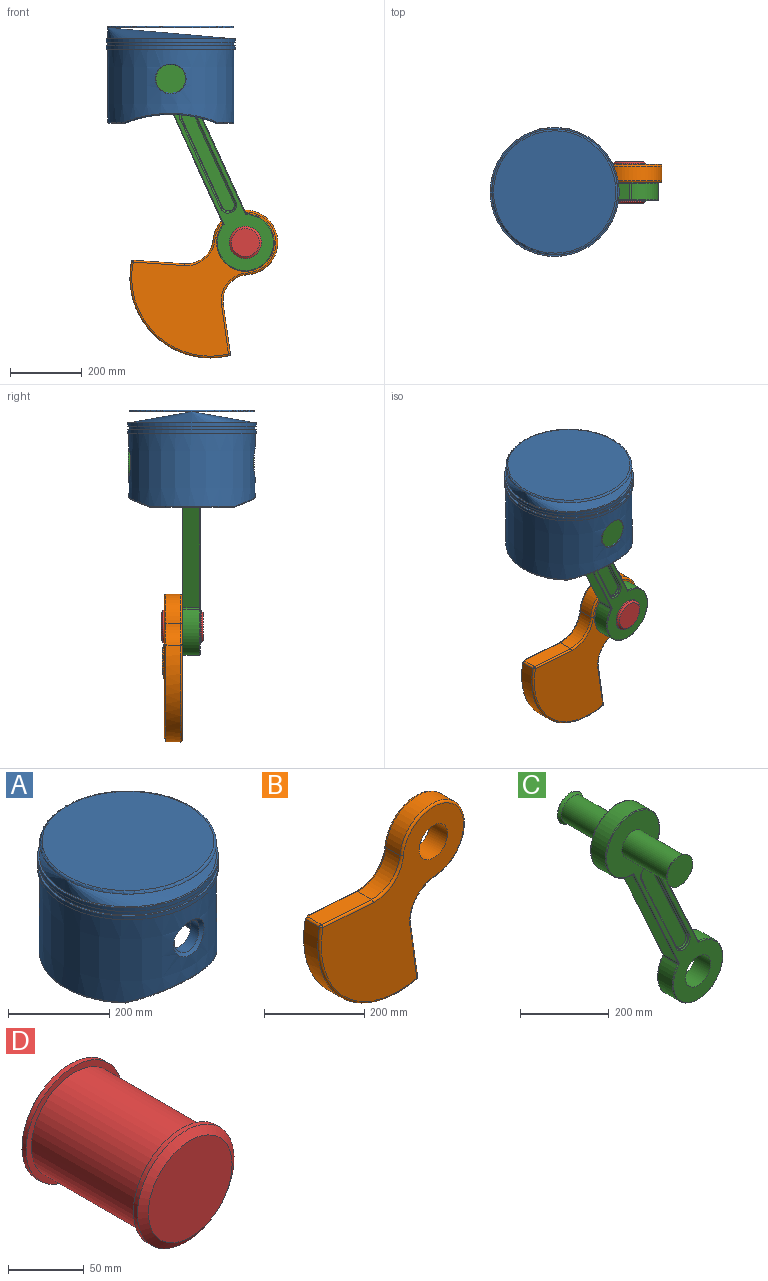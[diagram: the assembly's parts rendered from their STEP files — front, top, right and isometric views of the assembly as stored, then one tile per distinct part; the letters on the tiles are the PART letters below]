
ASSEMBLY  parts=4 mates=3
PART A: 29 faces, bbox 380.7x379x273.5 mm
  f0: cone r=175mm half-angle=0.2deg, axis (0,0,-1), area 12105mm2, adj f2,f7
  f1: plane 358.23x358.23mm, normal (0,0,1), area 4465.4mm2, adj f3,f5
  f2: plane 358.23x358.23mm, normal (0,0,-1), area 4437.3mm2, adj f0,f3
  f3: cylinder r=179.11mm len=358.23mm, axis (0,0,-1), area 10128.6mm2, adj f1,f2
  f4: plane 340.03x340.03mm, normal (0,0,1), area 90807.2mm2, adj f28
  f5: cone r=175mm half-angle=0.2deg, axis (0,0,-1), area 33563.3mm2, adj f1,f28
  f6: cylinder r=179.17mm len=358.34mm, axis (0,0,-1), area 10131.9mm2, adj f7,f8
  f7: plane 358.34x358.34mm, normal (0,0,1), area 4466.8mm2, adj f0,f6
  f8: plane 358.34x358.34mm, normal (0,0,-1), area 4438.7mm2, adj f6,f17
  f9: plane 291.53x291.53mm, normal (0,0,-1), area 66752.7mm2, adj f10
  f10: cylinder r=145.77mm len=291.53mm, axis (0,0,-1), area 181854.5mm2, adj f9,f15,f16,f24,f25,f26,f27
  f11: cylinder r=340mm len=251.53mm, axis (0,-1,0), area 7148.9mm2, adj f12,f14,f20,f25,f26,f27
  f12: plane 236.41x47.17mm, normal (0,0,-1), area 5172.1mm2, adj f11,f13,f20,f22,f23,f26
  f13: cylinder r=340mm len=251.53mm, axis (0,-1,0), area 7149.1mm2, adj f12,f14,f23,f24,f25,f26
  f14: plane 236.41x47.17mm, normal (0,0,-1), area 5172.1mm2, adj f11,f13,f20,f21,f23,f25
  f15: cylinder r=35mm len=70mm, axis (0,1,0), area 4846.2mm2, adj f10,f19
  f16: cylinder r=35mm len=70mm, axis (0,1,0), area 4846.2mm2, adj f10,f18
  f17: cone r=175mm half-angle=0.2deg, axis (0,0,-1), area 212035.7mm2, adj f8,f18,f19,f20,f21,f22,f23
  f18: bspline ~85.68x82.59mm, area 2302.6mm2, adj f16,f17
  f19: bspline ~85.68x82.59mm, area 2302.7mm2, adj f15,f17
  f20: bspline ~267.17x64.69mm, area 1460.4mm2, adj f11,f12,f14,f17,f21,f22
  f21: torus R=172.76mm, axis (0,0,1), area 1239.7mm2, adj f14,f17,f20,f23
  f22: torus R=172.76mm, axis (0,0,1), area 1239.7mm2, adj f12,f17,f20,f23
  f23: bspline ~267.17x64.69mm, area 1460.4mm2, adj f12,f13,f14,f17,f21,f22
  f24: bspline ~256.88x77.99mm, area 1310.8mm2, adj f10,f13,f25,f26
  f25: torus R=148.77mm, axis (0,0,1), area 772.3mm2, adj f10,f11,f13,f14,f24,f27
  f26: torus R=148.77mm, axis (0,0,1), area 772.3mm2, adj f10,f11,f12,f13,f24,f27
  f27: bspline ~256.88x77.99mm, area 1310.8mm2, adj f10,f11,f25,f26
  f28: torus R=170.01mm, axis (0,0,-1), area 8531.3mm2, adj f4,f5
PART B: 35 faces, bbox 450x60.6x491.2 mm
  f0: cylinder r=71.83mm len=81.86mm, axis (0,1,0), area 4750.8mm2, adj f1,f5,f21,f32
  f1: cylinder r=90mm len=179.84mm, axis (0,1,0), area 16411.5mm2, adj f0,f2,f19,f29
  f2: cylinder r=75mm len=79.87mm, axis (0,1,0), area 4637.4mm2, adj f1,f3,f18,f26
  f3: plane 142.02x40mm, normal (0.07,0,1), area 5677.6mm2, adj f2,f20,f22,f24,f25
  f4: cylinder r=223.85mm len=275.43mm, axis (0,1,0), area 17912.3mm2, adj f17,f22,f24,f27,f30,f31
  f5: plane 137.78x40mm, normal (0.99,0,0.14), area 5550.2mm2, adj f0,f23,f27,f30,f34
  f6: plane 401.08x401.08mm, normal (0,-1,0), area 75958.5mm2, adj f8,f25,f26,f29,f31,f32,f34
  f7: plane 392.34x392.34mm, normal (0,1,0), area 65113mm2, adj f8,f9,f17,f18,f19,f20,f21,f23
  f8: cylinder r=40mm len=80mm, axis (0,1,0), area 12566.4mm2, adj f6,f7
  f9: cylinder r=47.5mm len=95mm, axis (0,-1,0), area 895.4mm2, adj f7,f10
  f10: plane 95x95mm, normal (0,1,0), area 2670.4mm2, adj f9,f11
  f11: cylinder r=37.5mm len=75mm, axis (0,-1,0), area 706.9mm2, adj f10,f12
  f12: plane 75x75mm, normal (0,1,0), area 355.7mm2, adj f11,f14
  f13: plane 60x60mm, normal (0,1,0), area 2777.2mm2, adj f14,f16
  f14: cone r=30mm half-angle=50deg, axis (0,1,0), area 1611.9mm2, adj f12,f13
  f15: plane 2x2mm, normal (0,1,0), area 3.1mm2, adj f16
  f16: cone r=1mm half-angle=45deg, axis (0,1,0), area 66.6mm2, adj f13,f15
  f17: cone r=223.85mm half-angle=70deg, axis (0,-1,0), area 6357.7mm2, adj f4,f7,f20,f22,f23,f27
  f18: torus R=80mm, axis (0,-1,0), area 932.6mm2, adj f2,f7,f19,f20
  f19: torus R=85mm, axis (0,-1,0), area 3157.3mm2, adj f1,f7,f18,f21
  f20: cylinder r=5mm len=133.58mm, axis (-1,0,0.07), area 1046.3mm2, adj f3,f7,f17,f18,f22
  f21: torus R=76.83mm, axis (0,-1,0), area 956.4mm2, adj f0,f7,f19,f23
  f22: bspline ~80.83x33.21mm, area 98.9mm2, adj f3,f4,f17,f20,f24
  f23: cylinder r=5mm len=129.8mm, axis (-0.14,0,0.99), area 1021.6mm2, adj f5,f7,f17,f21,f27
  f24: cylinder r=5mm len=39.98mm, axis (0,1,0), area 278.7mm2, adj f3,f4,f22,f28
  f25: cylinder r=5mm len=142.37mm, axis (1,0,-0.07), area 1118.1mm2, adj f3,f6,f26,f28
  f26: torus R=80mm, axis (0,-1,0), area 932.6mm2, adj f2,f6,f25,f29
  f27: bspline ~123.64x49.12mm, area 100.3mm2, adj f4,f5,f17,f23,f30
  f28: sphere r=5mm, area 36.1mm2, adj f24,f25,f31
  f29: torus R=85mm, axis (0,-1,0), area 3157.3mm2, adj f1,f6,f26,f32
  f30: cylinder r=5mm len=39.99mm, axis (0,1,0), area 283.1mm2, adj f4,f5,f27,f33
  f31: torus R=218.85mm, axis (0,-1,0), area 3488.5mm2, adj f4,f6,f28,f33
  f32: torus R=76.83mm, axis (0,-1,0), area 956.4mm2, adj f0,f6,f29,f34
  f33: sphere r=5mm, area 38.3mm2, adj f30,f31,f34
  f34: cylinder r=5mm len=138.49mm, axis (0.14,0,-0.99), area 1093.1mm2, adj f5,f6,f32,f33
PART C: 61 faces, bbox 387.3x350x634.5 mm
  f0: plane 616.87x369.59mm, normal (0,-1,0), area 40935.7mm2, adj f17,f18,f19,f20,f21,f22,f39,f40
  f1: cylinder r=86mm len=172mm, axis (0,1,0), area 21255.5mm2, adj f35,f39,f44,f47
  f2: plane 312.28x142.52mm, normal (-0.91,0,-0.42), area 15790.1mm2, adj f36,f40,f47,f50
  f3: cylinder r=80mm len=160mm, axis (0,1,0), area 19516mm2, adj f38,f42,f50,f53
  f4: plane 312.28x142.52mm, normal (0.91,0,0.42), area 15790.1mm2, adj f37,f41,f44,f53
  f5: plane 616.87x369.59mm, normal (0,1,0), area 40935.7mm2, adj f16,f18,f27,f28,f29,f30,f35,f36
  f6: plane 245.63x112.1mm, normal (-0.91,0,-0.42), area 540mm2, adj f7,f9,f27,f32
  f7: cylinder r=20mm len=38.19mm, axis (0,1,0), area 125.7mm2, adj f6,f8,f29,f34
  f8: plane 245.63x112.1mm, normal (0.91,0,0.42), area 540mm2, adj f7,f9,f30,f33
  f9: cylinder r=20mm len=38.19mm, axis (0,1,0), area 125.7mm2, adj f6,f8,f28,f31
  f10: plane 279.63x146.1mm, normal (0,1,0), area 10087.9mm2, adj f31,f32,f33,f34
  f11: plane 245.63x112.1mm, normal (-0.91,0,-0.42), area 540mm2, adj f12,f14,f19,f23
  f12: cylinder r=20mm len=38.19mm, axis (0,-1,0), area 125.7mm2, adj f11,f13,f20,f24
  f13: plane 245.63x112.1mm, normal (0.91,0,0.42), area 540mm2, adj f12,f14,f22,f26
  f14: cylinder r=20mm len=38.19mm, axis (0,-1,0), area 125.7mm2, adj f11,f13,f21,f25
  f15: plane 279.63x146.1mm, normal (0,-1,0), area 10087.9mm2, adj f23,f24,f25,f26
  f16: cylinder r=35mm len=143mm, axis (0,1,0), area 31447.3mm2, adj f5,f59
  f17: cylinder r=35mm len=143mm, axis (0,1,0), area 31447.3mm2, adj f0,f60
  f18: cylinder r=40mm len=80mm, axis (0,1,0), area 12566.4mm2, adj f0,f5
  f19: cylinder r=3mm len=246.88mm, axis (0.42,0,-0.91), area 1272.3mm2, adj f0,f11,f20,f21
  f20: torus R=23mm, axis (0,-1,0), area 312.2mm2, adj f0,f12,f19,f22
  f21: torus R=23mm, axis (0,-1,0), area 312.2mm2, adj f0,f14,f19,f22
  f22: cylinder r=3mm len=246.88mm, axis (-0.42,0,0.91), area 1272.3mm2, adj f0,f13,f20,f21
  f23: cylinder r=3mm len=246.88mm, axis (-0.42,0,0.91), area 1272.3mm2, adj f11,f15,f24,f25
  f24: torus R=17mm, axis (0,-1,0), area 279.9mm2, adj f12,f15,f23,f26
  f25: torus R=17mm, axis (0,-1,0), area 279.9mm2, adj f14,f15,f23,f26
  f26: cylinder r=3mm len=246.88mm, axis (0.42,0,-0.91), area 1272.3mm2, adj f13,f15,f24,f25
  f27: cylinder r=3mm len=246.88mm, axis (0.42,0,-0.91), area 1272.3mm2, adj f5,f6,f28,f29
  f28: torus R=23mm, axis (0,-1,0), area 312.2mm2, adj f5,f9,f27,f30
  f29: torus R=23mm, axis (0,-1,0), area 312.2mm2, adj f5,f7,f27,f30
  f30: cylinder r=3mm len=246.88mm, axis (-0.42,0,0.91), area 1272.3mm2, adj f5,f8,f28,f29
  f31: torus R=17mm, axis (0,1,0), area 279.9mm2, adj f9,f10,f32,f33
  f32: cylinder r=3mm len=246.88mm, axis (0.42,0,-0.91), area 1272.3mm2, adj f6,f10,f31,f34
  f33: cylinder r=3mm len=246.88mm, axis (-0.42,0,0.91), area 1272.3mm2, adj f8,f10,f31,f34
  f34: torus R=17mm, axis (0,1,0), area 279.9mm2, adj f7,f10,f32,f33
  f35: torus R=84mm, axis (0,-1,0), area 1449.1mm2, adj f1,f5,f43,f46
  f36: cylinder r=2mm len=321.13mm, axis (0.42,0,-0.91), area 1088.3mm2, adj f2,f5,f46,f49
  f37: cylinder r=2mm len=321.13mm, axis (-0.42,0,0.91), area 1088.3mm2, adj f4,f5,f43,f52
  f38: torus R=78mm, axis (0,-1,0), area 1330mm2, adj f3,f5,f49,f52
  f39: torus R=84mm, axis (0,-1,0), area 1449.1mm2, adj f0,f1,f45,f48
  f40: cylinder r=2mm len=321.13mm, axis (-0.42,0,0.91), area 1088.3mm2, adj f0,f2,f48,f51
  f41: cylinder r=2mm len=321.13mm, axis (0.42,0,-0.91), area 1088.3mm2, adj f0,f4,f45,f54
  f42: torus R=78mm, axis (0,-1,0), area 1330mm2, adj f0,f3,f51,f54
  f43: bspline ~5.25x4.37mm, area 13mm2, adj f35,f37,f44
  f44: cylinder r=5mm len=46mm, axis (0,1,0), area 256.6mm2, adj f1,f4,f43,f45
  f45: bspline ~5.25x4.37mm, area 13mm2, adj f39,f41,f44
  f46: bspline ~4.92x4.42mm, area 13mm2, adj f35,f36,f47
  f47: cylinder r=5mm len=46mm, axis (0,1,0), area 256.6mm2, adj f1,f2,f46,f48
  f48: bspline ~4.92x4.42mm, area 13mm2, adj f39,f40,f47
  f49: bspline ~5.11x4.19mm, area 12.5mm2, adj f36,f38,f50
  f50: cylinder r=5mm len=46mm, axis (0,1,0), area 248.6mm2, adj f2,f3,f49,f51
  f51: bspline ~5.11x4.19mm, area 12.5mm2, adj f40,f42,f50
  f52: bspline ~4.77x4.27mm, area 12.5mm2, adj f37,f38,f53
  f53: cylinder r=5mm len=46mm, axis (0,1,0), area 248.6mm2, adj f3,f4,f52,f54
  f54: bspline ~4.77x4.27mm, area 12.5mm2, adj f41,f42,f53
  f55: cylinder r=41mm len=82mm, axis (0,1,0), area 257.6mm2, adj f56,f60
  f56: plane 82x82mm, normal (0,-1,0), area 5281mm2, adj f55
  f57: cylinder r=41mm len=82mm, axis (0,-1,0), area 257.6mm2, adj f58,f59
  f58: plane 82x82mm, normal (0,1,0), area 5281mm2, adj f57
  f59: cone r=41mm half-angle=45deg, axis (0,1,0), area 2026mm2, adj f16,f57
  f60: cone r=41mm half-angle=45deg, axis (0,-1,0), area 2026mm2, adj f17,f55
PART D: 9 faces, bbox 90x116x90 mm
  f0: cylinder r=40mm len=100mm, axis (0,1,0), area 25132.7mm2, adj f3,f6
  f1: cylinder r=45mm len=90mm, axis (0,1,0), area 1074.1mm2, adj f3,f7
  f2: plane 78x78mm, normal (0,-1,0), area 4778.4mm2, adj f7
  f3: plane 90x90mm, normal (0,1,0), area 1335.2mm2, adj f0,f1
  f4: cylinder r=45mm len=90mm, axis (0,-1,0), area 1074.1mm2, adj f6,f8
  f5: plane 78x78mm, normal (0,1,0), area 4778.4mm2, adj f8
  f6: plane 90x90mm, normal (0,-1,0), area 1335.2mm2, adj f0,f4
  f7: cone r=39mm half-angle=55deg, axis (0,1,0), area 1932.9mm2, adj f1,f2
  f8: cone r=39mm half-angle=55deg, axis (0,-1,0), area 1932.9mm2, adj f4,f5
PLACE A t=(-172.2,641.41,238.19)mm
PLACE B t=(-61.84,693.79,-313.91)mm
PLACE C t=(-172.2,643.79,238.19)mm
PLACE D t=(35.39,668.79,-216.68)mm
MATE fastened C.f3 <-> B.f1  axis (0,1,0) through (35.39,668.79,-216.68)mm
MATE cylindrical C.f16 <-> A.f15  axis (0,1,0) through (-172.2,740.29,238.19)mm
MATE fastened D.f0 <-> C.f3  axis (0,1,0) through (35.39,618.79,-216.68)mm
